FCSTD DOCUMENT  (FreeCAD 1.0R39285 (Git))
Label: USBPortMountPlate
License: All rights reserved
LicenseURL: https://en.wikipedia.org/wiki/All_rights_reserved
objects: Sketcher::SketchObject×1
note: 2 computed .brp shape members not serialized (recipe doc carries the construction recipe); baked Part::Feature solids carry a one-line shape summary decoded from their .brp

FEATURE [Sketcher::SketchObject] Sketch
  ArcFitTolerance = 1e-06
  FullyConstrained = true
  MakeInternals = false
  expr: Constraints[31] = 16.7 mm / 2 + 20 mm
  expr: Constraints[36] = 56.7 mm
  sketch-geometry (16):
    g0: Circle CenterX=-8.35 CenterY=0 CenterZ=0 NormalX=0 NormalY=0 NormalZ=1 AngleXU=0 Radius=1.5
    g1: Circle CenterX=8.35 CenterY=0 CenterZ=0 NormalX=0 NormalY=0 NormalZ=1 AngleXU=0 Radius=1.5
    g2: LineSegment StartX=-5.25 StartY=4 StartZ=0 EndX=5.25 EndY=4 EndZ=0
    g3: LineSegment StartX=-5.25 StartY=-4 StartZ=0 EndX=5.25 EndY=-4 EndZ=0
    g4: Circle CenterX=18.35 CenterY=0 CenterZ=0 NormalX=0 NormalY=0 NormalZ=1 AngleXU=0 Radius=1.5
    g5: Circle CenterX=-8.35 CenterY=0 CenterZ=0 NormalX=0 NormalY=0 NormalZ=1 AngleXU=0 Radius=2.5
    g6: LineSegment StartX=-5.25 StartY=4 StartZ=0 EndX=-5.25 EndY=-4 EndZ=0
    g7: LineSegment StartX=5.25 StartY=4 StartZ=0 EndX=5.25 EndY=-4 EndZ=0
    g8: Circle CenterX=8.35 CenterY=0 CenterZ=0 NormalX=0 NormalY=0 NormalZ=1 AngleXU=0 Radius=2.5
    g9: Circle CenterX=18.35 CenterY=0 CenterZ=0 NormalX=0 NormalY=0 NormalZ=1 AngleXU=0 Radius=2.5
    g10: LineSegment StartX=-28.35 StartY=10 StartZ=0 EndX=-28.35 EndY=-10 EndZ=0
    g11: LineSegment StartX=-28.35 StartY=-10 StartZ=0 EndX=28.35 EndY=-10 EndZ=0
    g12: LineSegment StartX=28.35 StartY=-10 StartZ=0 EndX=28.35 EndY=10 EndZ=0
    g13: LineSegment StartX=28.35 StartY=10 StartZ=0 EndX=-28.35 EndY=10 EndZ=0
    g14: Circle CenterX=-18.35 CenterY=0 CenterZ=0 NormalX=0 NormalY=0 NormalZ=1 AngleXU=0 Radius=1.5
    g15: Circle CenterX=-18.35 CenterY=0 CenterZ=0 NormalX=0 NormalY=0 NormalZ=1 AngleXU=0 Radius=2.5
  constraints (42):
    c: DistanceX(g0,g1) = 16.7
    c: Diameter(g1) = 3
    c: Equal(g0,g1)
    c: DistanceY(g0,g1) = 0
    c: Horizontal(g3)
    c: Distance(g2,g3) = 8
    c: DistanceX(g2,g2) = 10.5
    c: Symmetric(g3,g2,g-1)
    c: Symmetric(g0,g1,g-1)
    c: Equal(g1,g4)
    c: DistanceX(g1,g4) = 10
    c: Coincident(g5,g0)
    c: Coincident(g6,g2)
    c: Coincident(g6,g3)
    c: Vertical(g6)
    c: Coincident(g7,g2)
    c: Coincident(g7,g3)
    c: Vertical(g7)
    c: Equal(g2,g3)
    c: Equal(g6,g7)
    c: Diameter(g8) = 5
    c: Coincident(g4,g9)
    c: Coincident(g1,g8)
    c: Coincident(g10,g11)
    c: Coincident(g11,g12)
    c: Coincident(g12,g13)
    c: Coincident(g13,g10)
    c: Vertical(g10)
    c: Vertical(g12)
    c: Horizontal(g11)
    c: Horizontal(g13)
    c: Distance(g-1,g10) = 28.35
    c: DistanceY(g-1,g10) = 10
    c: DistanceY(g10,g10) = 20
    c: Equal(g8,g9)
    c: Equal(g9,g5)
    c: DistanceX(g11,g11) = 56.7
    c: Equal(g0,g14)
    c: Equal(g15,g5)
    c: Coincident(g14,g15)
    c: DistanceY(g-1,g14) = 0
    c: Distance(g14,g0) = 10
